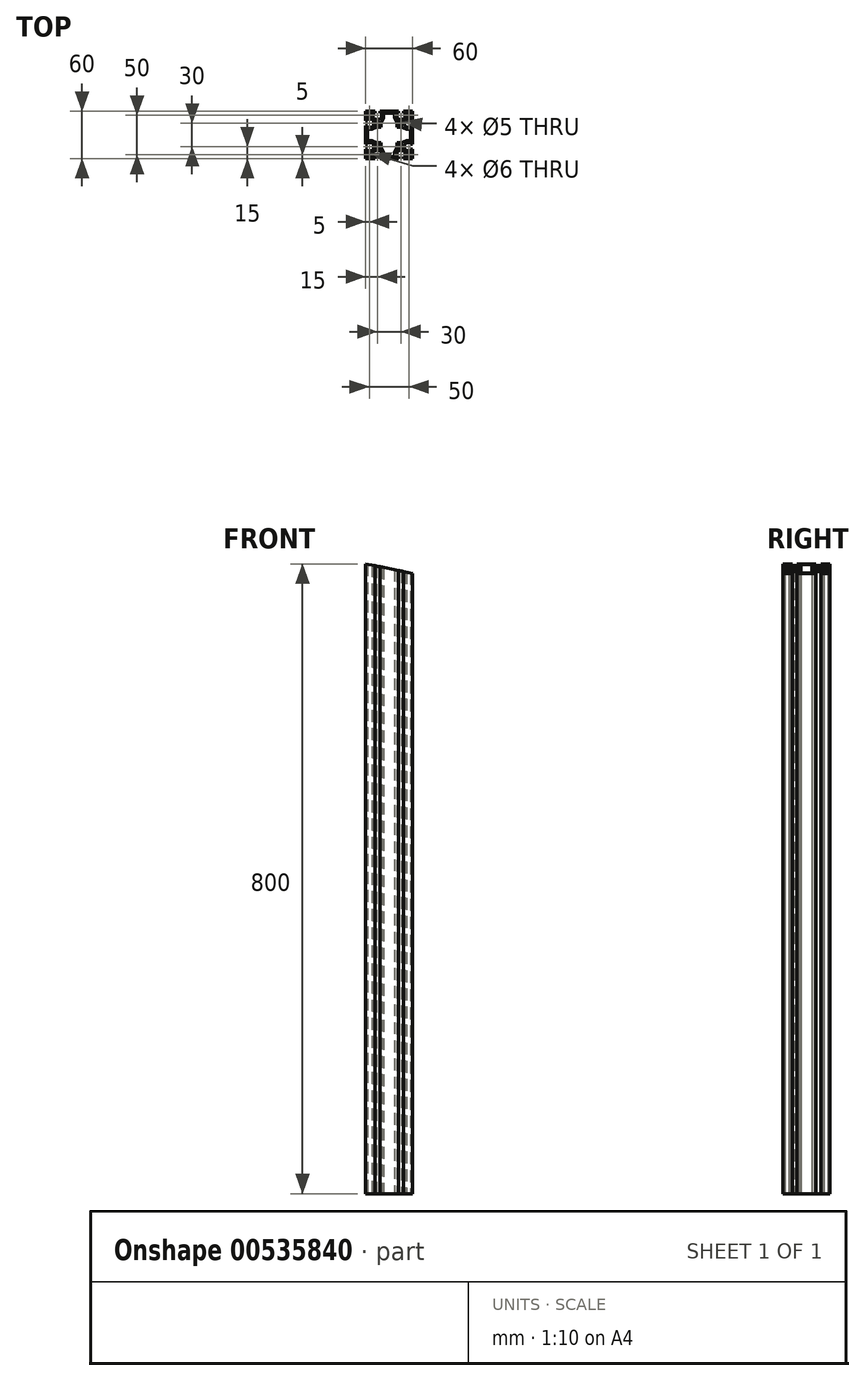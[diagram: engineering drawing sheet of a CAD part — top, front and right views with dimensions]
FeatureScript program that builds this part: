
annotation { "Feature Type Name" : "Feature", "Feature Type Description" : "" }
export const myFeature = defineFeature(function(context is Context, id is Id, definition is map)
    precondition{}
    {
        {
            var Q0;
            Q0=qCreatedBy(makeId("Top.planeOp"),FACE);
            var sketch = newSketch(context, id + "F0", { "sketchPlane" : qUnion([Q0])});
            skLineSegment(sketch, "E0.bottom", {"start": v(30, -30) * mm, "end": v(-30, -30) * mm});
            skLineSegment(sketch, "E0.top", {"start": v(30, 30) * mm, "end": v(-30, 30) * mm});
            skLineSegment(sketch, "E0.left", {"start": v(30, -30) * mm, "end": v(30, 30) * mm});
            skLineSegment(sketch, "E0.right", {"start": v(-30, -30) * mm, "end": v(-30, 30) * mm});
            skPoint(sketch, "E0.middle", {"position": v(0, 0) * mm});
            skLineSegment(sketch, "E1.top", {"start": v(-11.85, 30) * mm, "end": v(-18.15, 30) * mm});
            skLineSegment(sketch, "E1.left", {"start": v(-11.85, 27.5) * mm, "end": v(-11.85, 30) * mm});
            skLineSegment(sketch, "E1.right", {"start": v(-18.15, 27.5) * mm, "end": v(-18.15, 30) * mm});
            skPoint(sketch, "E1.middle", {"position": v(-15, 28.75) * mm});
            skLineSegment(sketch, "E2.bottom", {"start": v(-9.85, 27.5) * mm, "end": v(-11.85, 27.5) * mm});
            skLineSegment(sketch, "E2.left", {"start": v(-9.85, 27.5) * mm, "end": v(-9.85, 21.55) * mm});
            skLineSegment(sketch, "E2.right", {"start": v(-20.15, 27.5) * mm, "end": v(-20.15, 21.55) * mm});
            skPoint(sketch, "E2.middle", {"position": v(-15, 24.52) * mm});
            skArc(sketch, "E3", {"start": v(-20.15, 21.55) * mm, "mid": v(-15, 19.5) * mm, "end": v(-9.85, 21.55) * mm});
            skPoint(sketch, "E4.MirrorP", {"position": v(15, 24.52) * mm});
            skPoint(sketch, "E5.MirrorP", {"position": v(15, 28.75) * mm});
            skLineSegment(sketch, "E6.MirrorCS", {"start": v(11.85, 27.5) * mm, "end": v(11.85, 30) * mm});
            skLineSegment(sketch, "E7.MirrorCS", {"start": v(18.15, 27.5) * mm, "end": v(18.15, 30) * mm});
            skLineSegment(sketch, "E8.MirrorCS", {"start": v(9.85, 27.5) * mm, "end": v(11.85, 27.5) * mm});
            skLineSegment(sketch, "E9.MirrorCS", {"start": v(9.85, 27.5) * mm, "end": v(9.85, 21.55) * mm});
            skArc(sketch, "E10.MirrorCS", {"start": v(20.15, 21.55) * mm, "mid": v(15, 19.5) * mm, "end": v(9.85, 21.55) * mm});
            skLineSegment(sketch, "E11.MirrorCS", {"start": v(20.15, 27.5) * mm, "end": v(20.15, 21.55) * mm});
            skLineSegment(sketch, "E12.MirrorCS", {"start": v(11.85, 30) * mm, "end": v(18.15, 30) * mm});
            skLineSegment(sketch, "E13.1.0", {"start": v(27.5, 20.15) * mm, "end": v(21.55, 20.15) * mm});
            skLineSegment(sketch, "E13.1.1", {"start": v(27.5, 9.85) * mm, "end": v(21.55, 9.85) * mm});
            skArc(sketch, "E13.1.2", {"start": v(21.55, 20.15) * mm, "mid": v(19.5, 15) * mm, "end": v(21.55, 9.85) * mm});
            skLineSegment(sketch, "E13.1.3", {"start": v(27.5, -9.85) * mm, "end": v(21.55, -9.85) * mm});
            skLineSegment(sketch, "E13.1.4", {"start": v(27.5, -20.15) * mm, "end": v(21.55, -20.15) * mm});
            skPoint(sketch, "E13.1.5", {"position": v(28.75, 15) * mm});
            skPoint(sketch, "E13.1.6", {"position": v(28.75, -15) * mm});
            skArc(sketch, "E13.1.7", {"start": v(21.55, -20.15) * mm, "mid": v(19.5, -15) * mm, "end": v(21.55, -9.85) * mm});
            skPoint(sketch, "E13.1.8", {"position": v(24.52, -15) * mm});
            skPoint(sketch, "E13.1.9", {"position": v(24.52, 15) * mm});
            skLineSegment(sketch, "E13.1.10", {"start": v(27.5, 9.85) * mm, "end": v(27.5, 20.15) * mm});
            skLineSegment(sketch, "E13.1.11", {"start": v(27.5, -11.85) * mm, "end": v(27.5, -18.15) * mm});
            skLineSegment(sketch, "E13.1.12", {"start": v(30, 11.85) * mm, "end": v(30, 18.15) * mm});
            skLineSegment(sketch, "E13.1.13", {"start": v(30, -11.85) * mm, "end": v(30, -18.15) * mm});
            skLineSegment(sketch, "E13.1.14", {"start": v(27.5, 18.15) * mm, "end": v(30, 18.15) * mm});
            skLineSegment(sketch, "E13.1.15", {"start": v(27.5, 11.85) * mm, "end": v(30, 11.85) * mm});
            skLineSegment(sketch, "E13.1.16", {"start": v(27.5, 11.85) * mm, "end": v(27.5, 18.15) * mm});
            skLineSegment(sketch, "E13.1.17", {"start": v(27.5, -9.85) * mm, "end": v(27.5, -20.15) * mm});
            skLineSegment(sketch, "E13.1.18", {"start": v(27.5, -18.15) * mm, "end": v(30, -18.15) * mm});
            skLineSegment(sketch, "E13.1.19", {"start": v(27.5, -11.85) * mm, "end": v(30, -11.85) * mm});
            skLineSegment(sketch, "E13.2.0", {"start": v(20.15, -27.5) * mm, "end": v(20.15, -21.55) * mm});
            skLineSegment(sketch, "E13.2.1", {"start": v(9.85, -27.5) * mm, "end": v(9.85, -21.55) * mm});
            skArc(sketch, "E13.2.2", {"start": v(20.15, -21.55) * mm, "mid": v(15, -19.5) * mm, "end": v(9.85, -21.55) * mm});
            skLineSegment(sketch, "E13.2.3", {"start": v(-9.85, -27.5) * mm, "end": v(-9.85, -21.55) * mm});
            skLineSegment(sketch, "E13.2.4", {"start": v(-20.15, -27.5) * mm, "end": v(-20.15, -21.55) * mm});
            skPoint(sketch, "E13.2.5", {"position": v(15, -28.75) * mm});
            skPoint(sketch, "E13.2.6", {"position": v(-15, -28.75) * mm});
            skArc(sketch, "E13.2.7", {"start": v(-20.15, -21.55) * mm, "mid": v(-15, -19.5) * mm, "end": v(-9.85, -21.55) * mm});
            skPoint(sketch, "E13.2.8", {"position": v(-15, -24.52) * mm});
            skPoint(sketch, "E13.2.9", {"position": v(15, -24.52) * mm});
            skLineSegment(sketch, "E13.2.10", {"start": v(9.85, -27.5) * mm, "end": v(20.15, -27.5) * mm});
            skLineSegment(sketch, "E13.2.11", {"start": v(-11.85, -27.5) * mm, "end": v(-18.15, -27.5) * mm});
            skLineSegment(sketch, "E13.2.12", {"start": v(11.85, -30) * mm, "end": v(18.15, -30) * mm});
            skLineSegment(sketch, "E13.2.13", {"start": v(-11.85, -30) * mm, "end": v(-18.15, -30) * mm});
            skLineSegment(sketch, "E13.2.14", {"start": v(18.15, -27.5) * mm, "end": v(18.15, -30) * mm});
            skLineSegment(sketch, "E13.2.15", {"start": v(11.85, -27.5) * mm, "end": v(11.85, -30) * mm});
            skLineSegment(sketch, "E13.2.16", {"start": v(11.85, -27.5) * mm, "end": v(18.15, -27.5) * mm});
            skLineSegment(sketch, "E13.2.17", {"start": v(-9.85, -27.5) * mm, "end": v(-20.15, -27.5) * mm});
            skLineSegment(sketch, "E13.2.18", {"start": v(-18.15, -27.5) * mm, "end": v(-18.15, -30) * mm});
            skLineSegment(sketch, "E13.2.19", {"start": v(-11.85, -27.5) * mm, "end": v(-11.85, -30) * mm});
            skLineSegment(sketch, "E13.3.0", {"start": v(-27.5, -20.15) * mm, "end": v(-21.55, -20.15) * mm});
            skLineSegment(sketch, "E13.3.1", {"start": v(-27.5, -9.85) * mm, "end": v(-21.55, -9.85) * mm});
            skArc(sketch, "E13.3.2", {"start": v(-21.55, -20.15) * mm, "mid": v(-19.5, -15) * mm, "end": v(-21.55, -9.85) * mm});
            skLineSegment(sketch, "E13.3.3", {"start": v(-27.5, 9.85) * mm, "end": v(-21.55, 9.85) * mm});
            skLineSegment(sketch, "E13.3.4", {"start": v(-27.5, 20.15) * mm, "end": v(-21.55, 20.15) * mm});
            skPoint(sketch, "E13.3.5", {"position": v(-28.75, -15) * mm});
            skPoint(sketch, "E13.3.6", {"position": v(-28.75, 15) * mm});
            skArc(sketch, "E13.3.7", {"start": v(-21.55, 20.15) * mm, "mid": v(-19.5, 15) * mm, "end": v(-21.55, 9.85) * mm});
            skPoint(sketch, "E13.3.8", {"position": v(-24.52, 15) * mm});
            skPoint(sketch, "E13.3.9", {"position": v(-24.52, -15) * mm});
            skLineSegment(sketch, "E13.3.10", {"start": v(-27.5, -9.85) * mm, "end": v(-27.5, -20.15) * mm});
            skLineSegment(sketch, "E13.3.11", {"start": v(-27.5, 11.85) * mm, "end": v(-27.5, 18.15) * mm});
            skLineSegment(sketch, "E13.3.12", {"start": v(-30, -11.85) * mm, "end": v(-30, -18.15) * mm});
            skLineSegment(sketch, "E13.3.13", {"start": v(-30, 11.85) * mm, "end": v(-30, 18.15) * mm});
            skLineSegment(sketch, "E13.3.14", {"start": v(-27.5, -18.15) * mm, "end": v(-30, -18.15) * mm});
            skLineSegment(sketch, "E13.3.15", {"start": v(-27.5, -11.85) * mm, "end": v(-30, -11.85) * mm});
            skLineSegment(sketch, "E13.3.16", {"start": v(-27.5, -11.85) * mm, "end": v(-27.5, -18.15) * mm});
            skLineSegment(sketch, "E13.3.17", {"start": v(-27.5, 9.85) * mm, "end": v(-27.5, 20.15) * mm});
            skLineSegment(sketch, "E13.3.18", {"start": v(-27.5, 18.15) * mm, "end": v(-30, 18.15) * mm});
            skLineSegment(sketch, "E13.3.19", {"start": v(-27.5, 11.85) * mm, "end": v(-30, 11.85) * mm});
            skLineSegment(sketch, "E13.anchor1", {"start": v(0, 0) * mm, "end": v(-20.15, 21.55) * mm, "construction": true});
            skLineSegment(sketch, "E13.anchor2", {"start": v(0, 0) * mm, "end": v(-21.55, -20.15) * mm, "construction": true});
            skLineSegment(sketch, "E14.trimOffspring", {"start": v(-18.15, 27.5) * mm, "end": v(-20.15, 27.5) * mm});
            skLineSegment(sketch, "E15.trimOffspring", {"start": v(18.15, 27.5) * mm, "end": v(20.15, 27.5) * mm});
            skCircle(sketch, "E16", {"center": v(-15, 15) * mm, "radius": 2.5 * mm});
            skCircle(sketch, "E17", {"center": v(-25, 25) * mm, "radius": 3 * mm});
            skCircle(sketch, "E18.MirrorC", {"center": v(25, 25) * mm, "radius": 3 * mm});
            skCircle(sketch, "E19.MirrorC", {"center": v(25, -25) * mm, "radius": 3 * mm});
            skCircle(sketch, "E20.MirrorC", {"center": v(-25, -25) * mm, "radius": 3 * mm});
            skCircle(sketch, "E21.MirrorC", {"center": v(15, 15) * mm, "radius": 2.5 * mm});
            skCircle(sketch, "E22.MirrorC", {"center": v(15, -15) * mm, "radius": 2.5 * mm});
            skCircle(sketch, "E23.MirrorC", {"center": v(-15, -15) * mm, "radius": 2.5 * mm});
            skLineSegment(sketch, "E24", {"start": v(-7, 27.5) * mm, "end": v(0, 27.5) * mm});
            skLineSegment(sketch, "E25", {"start": v(-7, 27.5) * mm, "end": v(-7, 22) * mm});
            skLineSegment(sketch, "E26", {"start": v(-10, 10) * mm, "end": v(-10, 16) * mm});
            skLineSegment(sketch, "E27", {"start": v(-10, 16) * mm, "end": v(-7, 22) * mm});
            skLineSegment(sketch, "E28.MirrorCS", {"start": v(10, 10) * mm, "end": v(10, 16) * mm});
            skLineSegment(sketch, "E29.MirrorCS", {"start": v(10, 16) * mm, "end": v(7, 22) * mm});
            skLineSegment(sketch, "E30.MirrorCS", {"start": v(7, 27.5) * mm, "end": v(0, 27.5) * mm});
            skLineSegment(sketch, "E31.MirrorCS", {"start": v(7, 27.5) * mm, "end": v(7, 22) * mm});
            skLineSegment(sketch, "E32.1.0", {"start": v(-10, -10) * mm, "end": v(-16, -10) * mm});
            skLineSegment(sketch, "E32.1.1", {"start": v(-16, -10) * mm, "end": v(-22, -7) * mm});
            skLineSegment(sketch, "E32.1.2", {"start": v(-27.5, -7) * mm, "end": v(-22, -7) * mm});
            skLineSegment(sketch, "E32.1.3", {"start": v(-27.5, -7) * mm, "end": v(-27.5, 0) * mm});
            skLineSegment(sketch, "E32.1.4", {"start": v(-27.5, 7) * mm, "end": v(-27.5, 0) * mm});
            skLineSegment(sketch, "E32.1.5", {"start": v(-27.5, 7) * mm, "end": v(-22, 7) * mm});
            skLineSegment(sketch, "E32.1.6", {"start": v(-16, 10) * mm, "end": v(-22, 7) * mm});
            skLineSegment(sketch, "E32.1.7", {"start": v(-10, 10) * mm, "end": v(-16, 10) * mm});
            skLineSegment(sketch, "E32.2.0", {"start": v(10, -10) * mm, "end": v(10, -16) * mm});
            skLineSegment(sketch, "E32.2.1", {"start": v(10, -16) * mm, "end": v(7, -22) * mm});
            skLineSegment(sketch, "E32.2.2", {"start": v(7, -27.5) * mm, "end": v(7, -22) * mm});
            skLineSegment(sketch, "E32.2.3", {"start": v(7, -27.5) * mm, "end": v(0, -27.5) * mm});
            skLineSegment(sketch, "E32.2.4", {"start": v(-7, -27.5) * mm, "end": v(0, -27.5) * mm});
            skLineSegment(sketch, "E32.2.5", {"start": v(-7, -27.5) * mm, "end": v(-7, -22) * mm});
            skLineSegment(sketch, "E32.2.6", {"start": v(-10, -16) * mm, "end": v(-7, -22) * mm});
            skLineSegment(sketch, "E32.2.7", {"start": v(-10, -10) * mm, "end": v(-10, -16) * mm});
            skLineSegment(sketch, "E32.3.0", {"start": v(10, 10) * mm, "end": v(16, 10) * mm});
            skLineSegment(sketch, "E32.3.1", {"start": v(16, 10) * mm, "end": v(22, 7) * mm});
            skLineSegment(sketch, "E32.3.2", {"start": v(27.5, 7) * mm, "end": v(22, 7) * mm});
            skLineSegment(sketch, "E32.3.3", {"start": v(27.5, 7) * mm, "end": v(27.5, 0) * mm});
            skLineSegment(sketch, "E32.3.4", {"start": v(27.5, -7) * mm, "end": v(27.5, 0) * mm});
            skLineSegment(sketch, "E32.3.5", {"start": v(27.5, -7) * mm, "end": v(22, -7) * mm});
            skLineSegment(sketch, "E32.3.6", {"start": v(16, -10) * mm, "end": v(22, -7) * mm});
            skLineSegment(sketch, "E32.3.7", {"start": v(10, -10) * mm, "end": v(16, -10) * mm});
            skSolve(sketch);
        }
        {
            var Q0;
            {var subQ30=sQuery(id+"F0.wireOp",EDGE,"E1.left");Q0=makeQuery(id+"F0.imprint","IMPRINT",FACE,{"disambiguationData":[TD([[makeQuery(id+"F0.imprint","IMPRINT",EDGE,{"derivedFrom":subQ30}),-1.0]])]});}
            extrude(context, id + "F1", {"entities" : qUnion([Q0]), "depth" : 800 * mm, "offsetDistance" : 25 * mm});
        }
        {
            var Q0;
            Q0=makeQuery(id+"F1.opExtrude","SWEPT_EDGE",EDGE,{"disambiguationData":[OSD([sQuery(id+"F0.wireOp",EDGE,"E24"),sQuery(id+"F0.wireOp",EDGE,"E25")])]});
            var Q1;
            Q1=makeQuery(id+"F1.opExtrude","SWEPT_EDGE",EDGE,{"disambiguationData":[OSD([sQuery(id+"F0.wireOp",EDGE,"E30.MirrorCS"),sQuery(id+"F0.wireOp",EDGE,"E31.MirrorCS")])]});
            var Q2;
            Q2=makeQuery(id+"F1.opExtrude","SWEPT_EDGE",EDGE,{"disambiguationData":[OSD([sQuery(id+"F0.wireOp",EDGE,"840db5bc-c403-45cd-90c7-254e62d9e8c5.3.2"),sQuery(id+"F0.wireOp",EDGE,"840db5bc-c403-45cd-90c7-254e62d9e8c5.3.3")])]});
            var Q3;
            Q3=makeQuery(id+"F1.opExtrude","SWEPT_EDGE",EDGE,{"disambiguationData":[OSD([sQuery(id+"F0.wireOp",EDGE,"840db5bc-c403-45cd-90c7-254e62d9e8c5.3.4"),sQuery(id+"F0.wireOp",EDGE,"840db5bc-c403-45cd-90c7-254e62d9e8c5.3.5")])]});
            var Q4;
            Q4=makeQuery(id+"F1.opExtrude","SWEPT_EDGE",EDGE,{"disambiguationData":[OSD([sQuery(id+"F0.wireOp",EDGE,"840db5bc-c403-45cd-90c7-254e62d9e8c5.1.4"),sQuery(id+"F0.wireOp",EDGE,"840db5bc-c403-45cd-90c7-254e62d9e8c5.1.5")])]});
            var Q5;
            Q5=makeQuery(id+"F1.opExtrude","SWEPT_EDGE",EDGE,{"disambiguationData":[OSD([sQuery(id+"F0.wireOp",EDGE,"840db5bc-c403-45cd-90c7-254e62d9e8c5.1.2"),sQuery(id+"F0.wireOp",EDGE,"840db5bc-c403-45cd-90c7-254e62d9e8c5.1.3")])]});
            var Q6;
            Q6=makeQuery(id+"F1.opExtrude","SWEPT_EDGE",EDGE,{"disambiguationData":[OSD([sQuery(id+"F0.wireOp",EDGE,"840db5bc-c403-45cd-90c7-254e62d9e8c5.2.2"),sQuery(id+"F0.wireOp",EDGE,"840db5bc-c403-45cd-90c7-254e62d9e8c5.2.3")])]});
            var Q7;
            Q7=makeQuery(id+"F1.opExtrude","SWEPT_EDGE",EDGE,{"disambiguationData":[OSD([sQuery(id+"F0.wireOp",EDGE,"840db5bc-c403-45cd-90c7-254e62d9e8c5.2.4"),sQuery(id+"F0.wireOp",EDGE,"840db5bc-c403-45cd-90c7-254e62d9e8c5.2.5")])]});
            fillet(context, id + "F2", {"entities" : qUnion([Q0, Q1, Q2, Q3, Q4, Q5, Q6, Q7]), "radius" : 2 * mm, "tangentPropagation" : true, "allowEdgeOverflow" : false});
        }
        {
            var Q0;
            Q0=makeQuery(id+"F1.opExtrude","SWEPT_EDGE",EDGE,{"disambiguationData":[OSD([sQuery(id+"F0.wireOp",EDGE,"E26"),sQuery(id+"F0.wireOp",EDGE,"E27")])]});
            var Q1;
            Q1=makeQuery(id+"F1.opExtrude","SWEPT_EDGE",EDGE,{"disambiguationData":[OSD([sQuery(id+"F0.wireOp",EDGE,"E28.MirrorCS"),sQuery(id+"F0.wireOp",EDGE,"E29.MirrorCS")])]});
            var Q2;
            Q2=makeQuery(id+"F1.opExtrude","SWEPT_EDGE",EDGE,{"disambiguationData":[OSD([sQuery(id+"F0.wireOp",EDGE,"840db5bc-c403-45cd-90c7-254e62d9e8c5.3.0"),sQuery(id+"F0.wireOp",EDGE,"840db5bc-c403-45cd-90c7-254e62d9e8c5.3.1")])]});
            var Q3;
            Q3=makeQuery(id+"F1.opExtrude","SWEPT_EDGE",EDGE,{"disambiguationData":[OSD([sQuery(id+"F0.wireOp",EDGE,"840db5bc-c403-45cd-90c7-254e62d9e8c5.1.6"),sQuery(id+"F0.wireOp",EDGE,"840db5bc-c403-45cd-90c7-254e62d9e8c5.1.7")])]});
            var Q4;
            Q4=makeQuery(id+"F1.opExtrude","SWEPT_EDGE",EDGE,{"disambiguationData":[OSD([sQuery(id+"F0.wireOp",EDGE,"840db5bc-c403-45cd-90c7-254e62d9e8c5.1.0"),sQuery(id+"F0.wireOp",EDGE,"840db5bc-c403-45cd-90c7-254e62d9e8c5.1.1")])]});
            var Q5;
            Q5=makeQuery(id+"F1.opExtrude","SWEPT_EDGE",EDGE,{"disambiguationData":[OSD([sQuery(id+"F0.wireOp",EDGE,"840db5bc-c403-45cd-90c7-254e62d9e8c5.3.6"),sQuery(id+"F0.wireOp",EDGE,"840db5bc-c403-45cd-90c7-254e62d9e8c5.3.7")])]});
            var Q6;
            Q6=makeQuery(id+"F1.opExtrude","SWEPT_EDGE",EDGE,{"disambiguationData":[OSD([sQuery(id+"F0.wireOp",EDGE,"840db5bc-c403-45cd-90c7-254e62d9e8c5.2.0"),sQuery(id+"F0.wireOp",EDGE,"840db5bc-c403-45cd-90c7-254e62d9e8c5.2.1")])]});
            var Q7;
            Q7=makeQuery(id+"F1.opExtrude","SWEPT_EDGE",EDGE,{"disambiguationData":[OSD([sQuery(id+"F0.wireOp",EDGE,"840db5bc-c403-45cd-90c7-254e62d9e8c5.2.6"),sQuery(id+"F0.wireOp",EDGE,"840db5bc-c403-45cd-90c7-254e62d9e8c5.2.7")])]});
            fillet(context, id + "F3", {"entities" : qUnion([Q0, Q1, Q2, Q3, Q4, Q5, Q6, Q7]), "radius" : 7 * mm, "tangentPropagation" : true, "allowEdgeOverflow" : false});
        }
        {
            var Q0;
            {var subQ0=sQuery(id+"F0.wireOp",EDGE,"E0.bottom");Q0=makeQuery(id+"F1.opExtrude","SWEPT_FACE",FACE,{"disambiguationData":[OSD([subQ0]),TDD([makeQuery(id+"F0.imprint","IMPRINT",EDGE,{"disambiguationData":[TD([[makeQuery(id+"F0.imprint","INTERSECT",VERTEX,{"derivedFrom":[subQ0,sQuery(id+"F0.wireOp",EDGE,"E13.2.12"),sQuery(id+"F0.wireOp",EDGE,"E13.2.15")]}),-1.0]])],"derivedFrom":subQ0})])]});}
            var sketch = newSketch(context, id + "F4", { "sketchPlane" : qUnion([Q0])});
            skLineSegment(sketch, "E33.0", {"start": v(-18.15, 800) * mm, "end": v(-30, 800) * mm});
            skLineSegment(sketch, "E33.1", {"start": v(30, 800) * mm, "end": v(30, 0) * mm});
            skLineSegment(sketch, "E34", {"start": v(-30, 800) * mm, "end": v(30, 800) * mm});
            skLineSegment(sketch, "E35", {"start": v(30, 740) * mm, "end": v(-30, 800) * mm});
            skLineSegment(sketch, "E36.0", {"start": v(-18.15, 0) * mm, "end": v(-30, 0) * mm});
            skLineSegment(sketch, "E37", {"start": v(-30, 0) * mm, "end": v(30, 0) * mm});
            skLineSegment(sketch, "E38", {"start": v(30, 60) * mm, "end": v(-30, 0) * mm});
            skSolve(sketch);
        }
        {
            var Q0;
            Q0=qCreatedBy(makeId("Front.planeOp"),FACE);
            var sketch = newSketch(context, id + "F5", { "sketchPlane" : qUnion([Q0])});
            skLineSegment(sketch, "E39.bottom", {"start": v(113.94, 882.4) * mm, "end": v(-8.75, 906.81) * mm});
            skLineSegment(sketch, "E39.top", {"start": v(92.7, 775.6) * mm, "end": v(-30, 800) * mm});
            skLineSegment(sketch, "E39.left", {"start": v(113.94, 882.4) * mm, "end": v(92.7, 775.6) * mm});
            skLineSegment(sketch, "E39.right", {"start": v(-8.75, 906.81) * mm, "end": v(-30, 800) * mm});
            skSolve(sketch);
        }
        {
            var Q0;
            Q0 = qSketchRegion(id + "F5", true);
            extrude(context, id + "F6", {"entities" : qUnion([Q0]), "operationType" : NewBodyOperationType.REMOVE, "depth" : 30 * mm, "offsetDistance" : 25 * mm, "hasSecondDirection" : true, "secondDirectionOppositeDirection" : true, "secondDirectionDepth" : 30 * mm});
        }
    });
